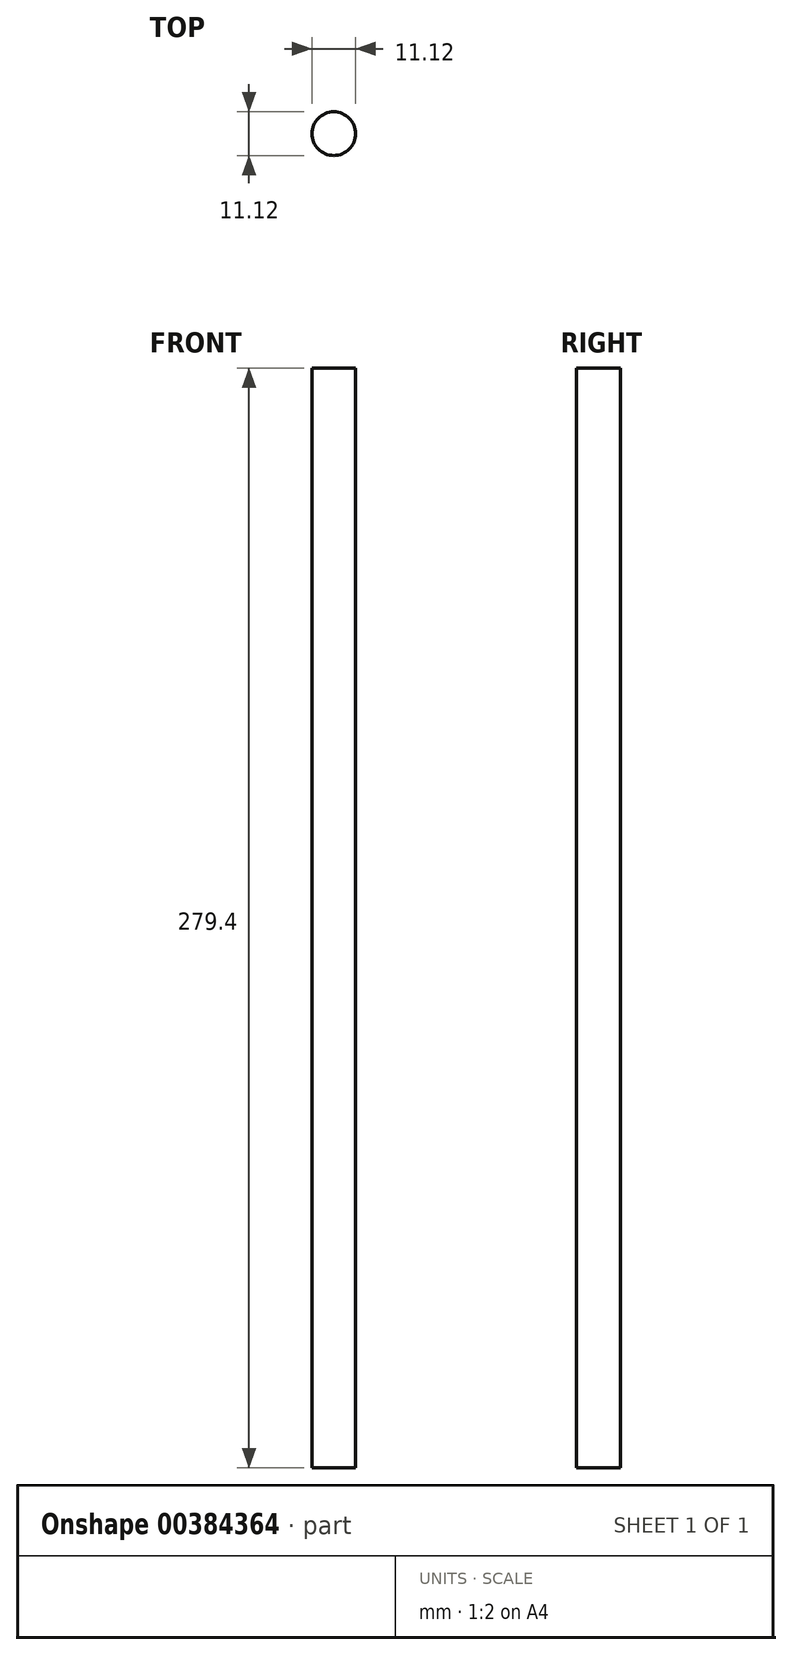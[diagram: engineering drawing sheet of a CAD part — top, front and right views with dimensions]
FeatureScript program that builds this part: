
annotation { "Feature Type Name" : "Feature", "Feature Type Description" : "" }
export const myFeature = defineFeature(function(context is Context, id is Id, definition is map)
    precondition{}
    {
        {
            var Q0;
            Q0=qCreatedBy(makeId("Top.planeOp"),FACE);
            var sketch = newSketch(context, id + "F0", { "sketchPlane" : qUnion([Q0])});
            skCircle(sketch, "E0", {"center": v(0, 0) * mm, "radius": 5.56 * mm});
            skSolve(sketch);
        }
        {
            var Q0;
            Q0 = qSketchRegion(id + "F0", true);
            extrude(context, id + "F1", {"entities" : qUnion([Q0]), "oppositeDirection" : true, "depth" : 279.4 * mm, "offsetDistance" : 25.4 * mm});
        }
    });
